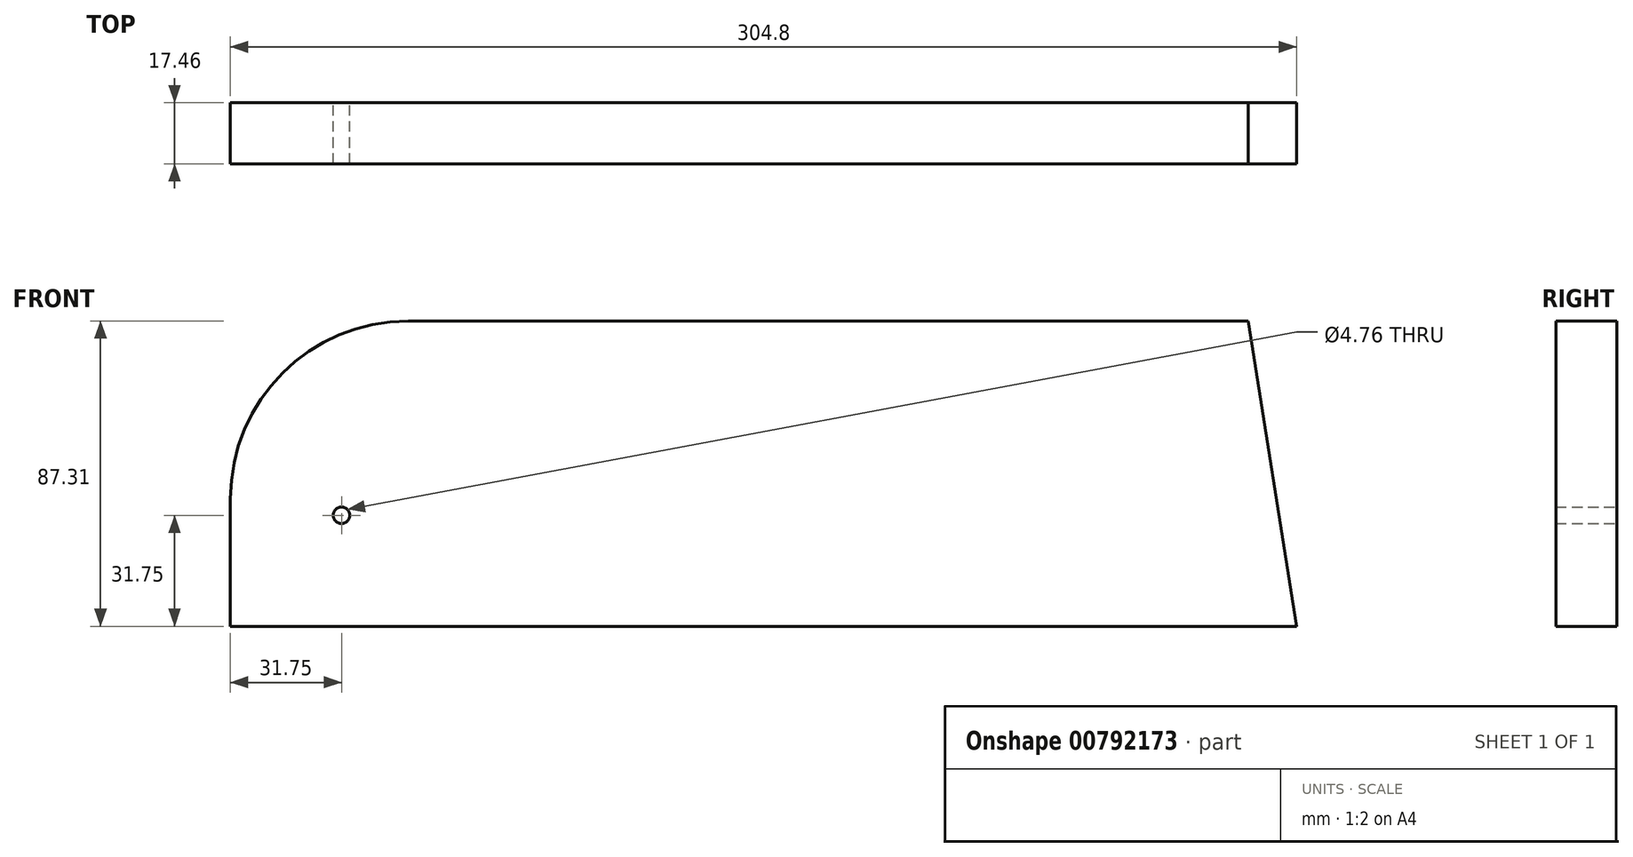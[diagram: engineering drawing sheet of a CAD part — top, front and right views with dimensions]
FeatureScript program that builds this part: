
annotation { "Feature Type Name" : "Feature", "Feature Type Description" : "" }
export const myFeature = defineFeature(function(context is Context, id is Id, definition is map)
    precondition{}
    {
        {
            var Q0;
            Q0=qCreatedBy(makeId("Front.planeOp"),FACE);
            var sketch = newSketch(context, id + "F0", { "sketchPlane" : qUnion([Q0])});
            skLineSegment(sketch, "E0.bottom", {"start": v(0, 0) * mm, "end": v(-304.8, 0) * mm});
            skLineSegment(sketch, "E0.top", {"start": v(-13.83, 87.31) * mm, "end": v(-254, 87.31) * mm});
            skLineSegment(sketch, "E0.right", {"start": v(-304.8, 0) * mm, "end": v(-304.8, 36.51) * mm});
            skPoint(sketch, "E1.visualSharp", {"position": v(-304.8, 87.31) * mm});
            skArc(sketch, "E1.filletArc", {"start": v(-254, 87.31) * mm, "mid": v(-289.92, 72.43) * mm, "end": v(-304.8, 36.51) * mm});
            skLineSegment(sketch, "E2", {"start": v(0, 0) * mm, "end": v(-13.83, 87.31) * mm});
            skCircle(sketch, "E3", {"center": v(-273.05, 31.75) * mm, "radius": 2.38 * mm});
            skSolve(sketch);
        }
        {
            var Q0;
            Q0=makeQuery(id+"F0.imprint","IMPRINT",FACE,{"disambiguationData":[TD([[makeQuery(id+"F0.imprint","IMPRINT",EDGE,{"derivedFrom":sQuery(id+"F0.wireOp",EDGE,"E0.bottom")}),-1.0]])]});
            extrude(context, id + "F1", {"entities" : qUnion([Q0]), "depth" : 17.46 * mm, "offsetDistance" : 25.4 * mm});
        }
    });
